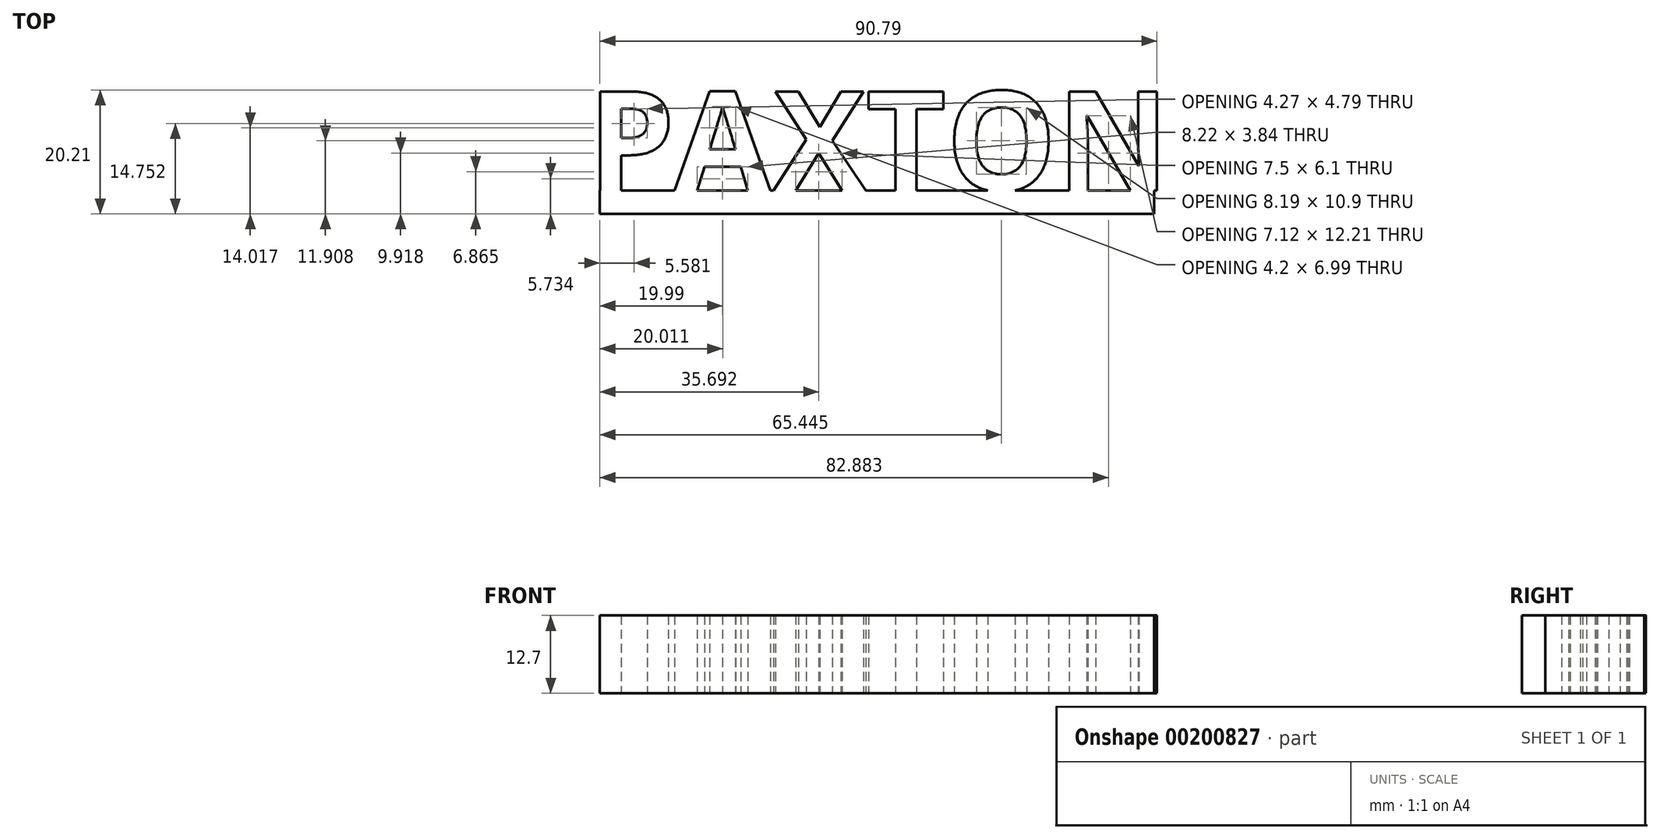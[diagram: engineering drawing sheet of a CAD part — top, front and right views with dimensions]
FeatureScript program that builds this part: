
annotation { "Feature Type Name" : "Feature", "Feature Type Description" : "" }
export const myFeature = defineFeature(function(context is Context, id is Id, definition is map)
    precondition{}
    {
        {
            var Q0;
            Q0=qCreatedBy(makeId("Top.planeOp"),FACE);
            var sketch = newSketch(context, id + "F0", { "sketchPlane" : qUnion([Q0])});
            skText(sketch, "E0", { "text": "PAXTON", "fontName": "OpenSans-Bold.ttf"});
            skLineSegment(sketch, "E1", {"start": v(261.51, -47.47) * mm, "end": v(261.51, -51.28) * mm});
            skLineSegment(sketch, "E2", {"start": v(351.84, -47.47) * mm, "end": v(351.84, -51.27) * mm});
            skLineSegment(sketch, "E3", {"start": v(351.84, -51.27) * mm, "end": v(261.51, -51.28) * mm});
            skLineSegment(sketch, "E4", {"start": v(261.51, -47.47) * mm, "end": v(351.84, -47.47) * mm});
            const initialGuessF0  = {"E0": [0.2595, -0.04747, 1, 0, 0.01628]};
            skSetInitialGuess(sketch, initialGuessF0);
            skSolve(sketch);
        }
        {
            var Q0;
            Q0 = qSketchRegion(id + "F0", true);
            extrude(context, id + "F1", {"entities" : qUnion([Q0]), "depth" : 12.7 * mm});
        }
    });
